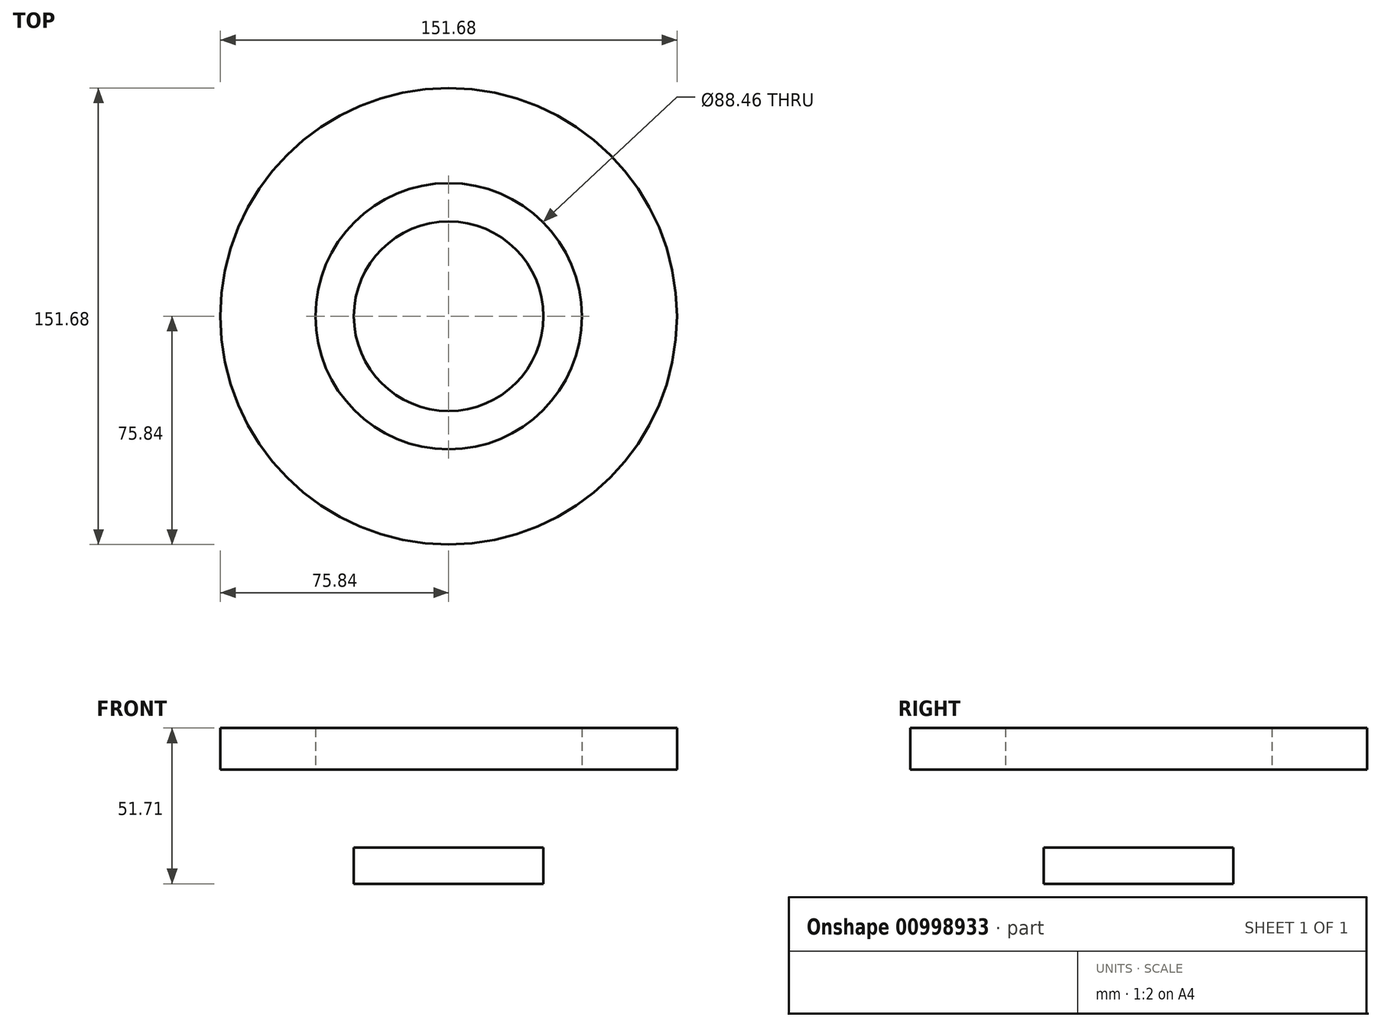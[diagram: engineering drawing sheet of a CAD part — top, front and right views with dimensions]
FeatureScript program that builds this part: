
annotation { "Feature Type Name" : "Feature", "Feature Type Description" : "" }
export const myFeature = defineFeature(function(context is Context, id is Id, definition is map)
    precondition{}
    {
        {
            var Q0;
            Q0=qCreatedBy(makeId("Front.planeOp"),FACE);
            var sketch = newSketch(context, id + "F0", { "sketchPlane" : qUnion([Q0])});
            skLineSegment(sketch, "E0.bottom", {"start": v(0, 0) * mm, "end": v(31.49, 0) * mm});
            skLineSegment(sketch, "E0.top", {"start": v(0, 12) * mm, "end": v(31.49, 12) * mm});
            skLineSegment(sketch, "E0.left", {"start": v(0, 0) * mm, "end": v(0, 12) * mm});
            skLineSegment(sketch, "E0.right", {"start": v(31.49, 0) * mm, "end": v(31.49, 12) * mm});
            skLineSegment(sketch, "E1.bottom", {"start": v(44.23, 37.98) * mm, "end": v(75.84, 37.98) * mm});
            skLineSegment(sketch, "E1.top", {"start": v(44.23, 51.7) * mm, "end": v(75.84, 51.7) * mm});
            skLineSegment(sketch, "E1.left", {"start": v(44.23, 37.98) * mm, "end": v(44.23, 51.7) * mm});
            skLineSegment(sketch, "E1.right", {"start": v(75.84, 37.98) * mm, "end": v(75.84, 51.7) * mm});
            skLineSegment(sketch, "E2", {"start": v(0, 0) * mm, "end": v(0, 70.33) * mm, "construction": true});
            skSolve(sketch);
        }
        {
            var Q0;
            Q0=makeQuery(id+"F0.imprint","IMPRINT",FACE,{"disambiguationData":[TD([[makeQuery(id+"F0.imprint","IMPRINT",EDGE,{"derivedFrom":sQuery(id+"F0.wireOp",EDGE,"E1.bottom")}),1.0]])]});
            var Q1;
            Q1=makeQuery(id+"F0.imprint","IMPRINT",FACE,{"disambiguationData":[TD([[makeQuery(id+"F0.imprint","IMPRINT",EDGE,{"derivedFrom":sQuery(id+"F0.wireOp",EDGE,"E0.bottom")}),1.0]])]});
            var Q2;
            Q2=sQuery(id+"F0.wireOp",EDGE,"E2");
            var Q3;
            Q3=sQuery(id+"F0.wireOp",EDGE,"E2");
            revolve(context, id + "F1", {"surfaceOperationType" : NewSurfaceOperationType.NEW, "entities" : qUnion([Q0, Q1]), "surfaceEntities" : qUnion([Q2]), "axis" : qUnion([Q3]), "revolveType" : RevolveType.FULL});
        }
    });
